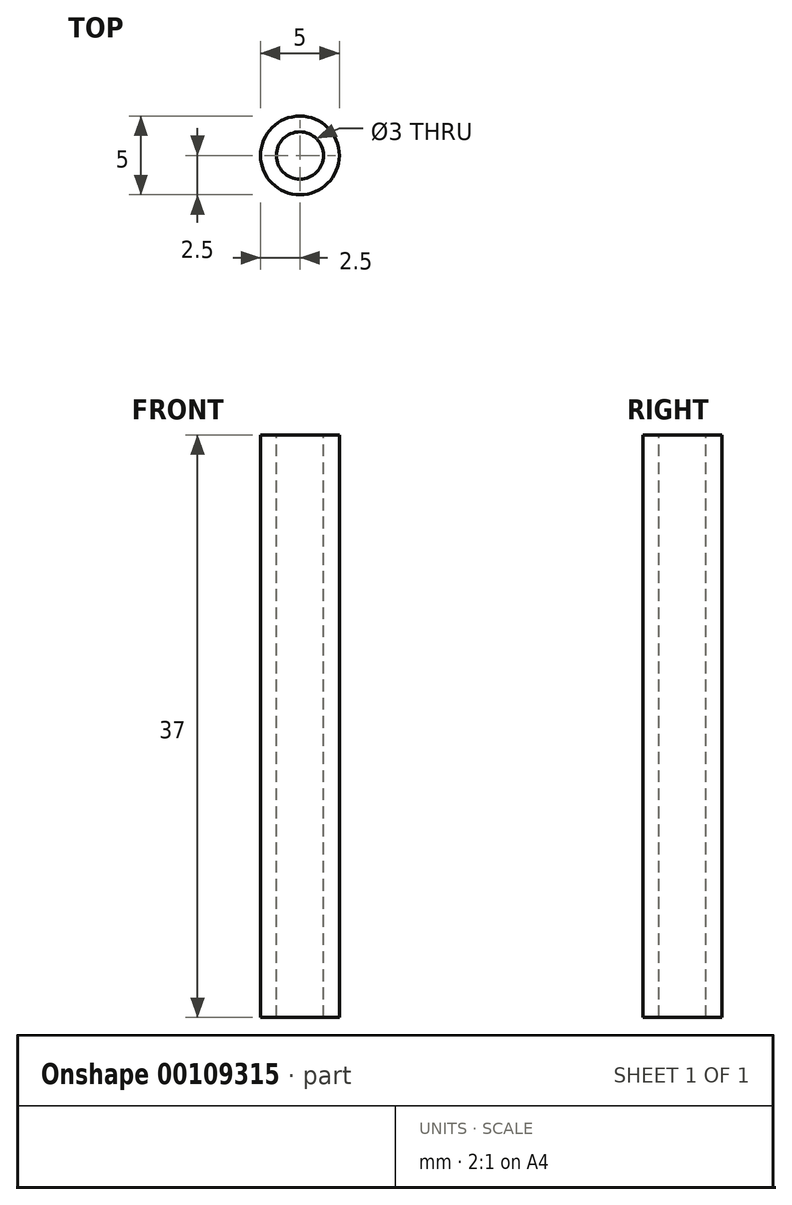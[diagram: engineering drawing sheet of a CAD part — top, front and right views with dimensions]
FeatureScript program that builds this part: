
annotation { "Feature Type Name" : "Feature", "Feature Type Description" : "" }
export const myFeature = defineFeature(function(context is Context, id is Id, definition is map)
    precondition{}
    {
        {
            var Q0;
            Q0=qCreatedBy(makeId("Top.planeOp"),FACE);
            var sketch = newSketch(context, id + "F0", { "sketchPlane" : qUnion([Q0])});
            skCircle(sketch, "E0", {"center": v(0, 0) * mm, "radius": 2.5 * mm});
            skSolve(sketch);
        }
        {
            var Q0;
            Q0=makeQuery(id+"F0.imprint","IMPRINT",FACE,{"disambiguationData":[TD([[makeQuery(id+"F0.imprint","IMPRINT",EDGE,{"derivedFrom":sQuery(id+"F0.wireOp",EDGE,"E0")}),1.0]])]});
            extrude(context, id + "F1", {"entities" : qUnion([Q0]), "depth" : 37 * mm});
        }
        {
            var Q0;
            Q0=makeQuery(id+"F1.opExtrude","CAP_FACE",FACE,{"disambiguationData":[OSD([sQuery(id+"F0.wireOp",EDGE,"E0")])],"isStart":false});
            var sketch = newSketch(context, id + "F2", { "sketchPlane" : qUnion([Q0])});
            skCircle(sketch, "E1", {"center": v(0, 0) * mm, "radius": 1.5 * mm});
            skSolve(sketch);
        }
        {
            var Q0;
            Q0 = qSketchRegion(id + "F2", true);
            extrude(context, id + "F3", {"entities" : qUnion([Q0]), "operationType" : NewBodyOperationType.REMOVE, "endBound" : BoundingType.THROUGH_ALL, "oppositeDirection" : true, "depth" : 25.4 * mm});
        }
    });
